# Revit family: mingata_midi_612202_0031_1_76_161c
name_source: partatom
category: Lighting Fixtures
units: mm (PartAtom-declared; Revit-internal decimal feet)

## family parameters
Cut with Voids When Loaded = No
Host = Face
Light Source = No
Part Type = Normal
Room Calculation Point = No
Round Connector Dimension = Use Diameter
Shared = No

## types (1)
- MINGATA midi (1 x LED Modul 740, 12000 lm, 4000)
    Apparent Load = 84 VA
    CIE Flux Codes = 40 76 97 100 100
    Color Rendering = 70
    Color Temperature = 4000
    Default Elevation = 1800 mm
    Description = Series: MINGATA midi
Functional pole-side and pole-top luminaire in a modern design. Housing made of corrosion-resistant die-cast aluminium, seawater resistant powder-coated. Pole-top fixing with integrated cable routing and stainless steel screws. With membrane valve as a standard to avoid condensed water. Cover clear single-pane toughened glass. Asymmetrical light distribution for M, P and C lighting classes. Luminaires for spigot Ø 42 mm. Tool-free maintenance / replacement by Eccentric-Lock system with disconnect plug and Hybrid-Lock-System. 4 x 1.0 mm² connecting cable included, length 8 m. 
Colour: anthracite metallic (DB703)
Length: 700 mm
Width: 340 mm
Height: 100 mm
Lamp: LED
System power: 84 W
Rated luminous flux: 12000 lm
Luminous efficiency: 143 lm/W
Control gear: Converter, dimmable, DALI
Protection class: II
Type of protection: IP 66
    Height = 100 mm  [stored 0.328084 ft]
    Lamp = 1 x LED Modul 740
    Lamp Light Flux = 12000 lm
    Lamp count = 1
    Length = 700 mm
    Lifetime = 50000 h
    Luminous efficacy = 143 lm/W
    Manufacturer = RZB
    ModVariant = No
    Model = 612202.0031.1.76
    Mounting Place = Pole
    Mounting Type = Pole top
    Number of Poles = 1
    OnlyDefault = Yes
    Power Factor = 1
    Product Name = MINGATA midi
    Product group = Pole luminaires
    ProductGroupID = 1352
    Protection Class = Protection class II
    Protection Degree = IP 66
    RLX_Detail_Level = 1
    RLX_Emergency_Light_Flux = 0 lm
    RLX_Emergency_Type = 0
    RLX_Emergency_Type_DB = No
    RlxData = <blob elided: 50657 chars, md5=a346af56>
    Socket = socket
    Standby Power = 0 W
    System Light Flux = 12000 lm
    System Power = 84 W
    Type Comments = ALEA SPOT
    Type Image = 612181.0031.1.76.jpg
    URL = http://relux.com
    VarID = ---
    Voltage = 230 V
    Voltage Range = 220-240 V
    Weight = 0.00 kg
    Width = 340 mm

note: [stored X ft] marks values corroborated as IEEE doubles in the binary element streams (Revit-internal decimal feet)

## geometry (parser evidence)
native form markers: Sweep x11
no freeform markers — native parametric forms only
